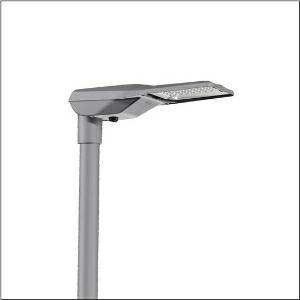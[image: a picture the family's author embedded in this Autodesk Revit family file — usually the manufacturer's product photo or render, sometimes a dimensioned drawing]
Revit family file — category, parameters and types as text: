
# Revit family: streetlight_sl_21_mini___p0_8ab_5xe2r33r08hb_51e7
name_source: partatom
category: Lighting Fixtures
units: mm (PartAtom-declared; Revit-internal decimal feet)

## family parameters
Cut with Voids When Loaded = No
Host = Face
Light Source = No
Part Type = Normal
Room Calculation Point = No
Round Connector Dimension = Use Diameter
Shared = No

## types (1)
- --- (1 x LED, 7850 lm, 66 W, 3000K)
    Apparent Load = 66 VA
    CIE Flux Codes = 36 71 98 100 100
    Color Rendering = 70
    Color Temperature = 3000K
    Default Elevation = 1800 mm
    Description = Streetlight SL 21 mini, mast luminaire, primary light control with lens, of PMMA, primary optical cover: cover, of toughened safety glass, transparent, light distribution: P0.8aB, light emission: direct distribution, primary light characteristic: asymmetric, installation type: post-top, side-entry, LED, High Power LED, rated luminous flux: 7.850lm, luminous efficacy: 119lm/W, light colour: 730, colour temperature: 3000K, control gear: D4i, control: pre-setting: logarithmic dimming characteristic, flexible luminous flux parameterisation, time-dependent luminous flux control, constant luminous flux control, overheat protection, mains connection: 220..240V, AC, 50/60Hz, start of lifetime: 66W, end of service life: 69W, reduction: 30W, luminaire housing, of diecast aluminium, powder-coated, SITECO metallic grey (DB 702S), corrosivity category C5 high according to DIN EN ISO 12944, multi-level sealing system, sealing non-destructively replaceable, inclination adjustable: 0°, 5°, 10°, 15°, please order mast flange separately, length: 628mm, width: 235mm, height: 110mm, mast flange for spigot size: 42mm (side-entry): 5XC10008XM4, 60/48mm (side-entry/post-top): 5XC10108XM2, 76/60mm (side-entry/post-top): 5XC10108XM1, mounting height: 4..8m, Smart Interface below, protection rating (complete): IP66, insulation class (complete): insulation class II (safety insulation), certification: CE, ENEC, ENEC+, VDE, impact resistance: IK10, permissible operating ambient temperature for outdoor applications: -40..+50°C, standard-compliant lighting for roads and squares, packaging unit: 1 piece

Light Distribution: P0.8aB
    Height = 110 mm
    Lamp = 1 x LED
    Lamp Light Flux = 7850 lm
    Lamp Power = 66 W
    Lamp count = 1
    Length = 625 mm
    Luminous efficacy = 119 lm/W
    Manufacturer = Siteco
    ModVariant = No
    Model = 5XE2R33R08HB
    Number of Poles = 1
    OnlyDefault = Yes
    Power Factor = 1
    Product Name = Streetlight SL 21 mini | P0.8aB
    Product group = mast luminaire | pylon top
    ProductGroupID = 6100
    Protection Class = Protection class II
    Protection Degree = IP 66
    RLX_Detail_Level = 1
    RLX_Emergency_Light_Flux = 0 lm
    RLX_Emergency_Type = 0
    RLX_Emergency_Type_DB = No
    RlxData = <blob elided: 92533 chars, md5=b5e59772>
    Socket = socket
    Standby Power = 0 W
    System Light Flux = 7850 lm
    System Power = 66 W
    Type Comments = factory setting: luminous flux: 100 % | dim-lin: 254 | 670 mA
    Type Image = l_1003516.jpg
    URL = http://relux.com
    VarID = @adj_082673
    Voltage = 0 V
    Weight = 0.00 kg
    Width = 234 mm

## geometry (parser evidence)
native form markers: Blend x4, Sweep x9
no freeform markers — native parametric forms only
